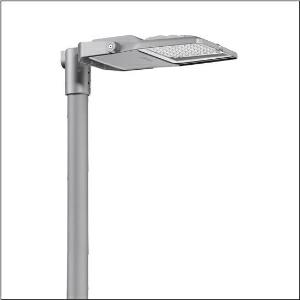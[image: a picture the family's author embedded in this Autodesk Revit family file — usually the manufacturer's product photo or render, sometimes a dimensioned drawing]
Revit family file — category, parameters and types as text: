
# Revit family: floodlight_fl_21_iq_mini___pl43_5xa7771d2a3a_a639
name_source: partatom
category: Lighting Fixtures
units: mm (PartAtom-declared; Revit-internal decimal feet)

## family parameters
Cut with Voids When Loaded = No
Host = Face
Light Source = No
Part Type = Normal
Room Calculation Point = No
Round Connector Dimension = Use Diameter
Shared = No

## types (1)
- --- (1 x LED, 18290 lm, 143 W, 3000K)
    Apparent Load = 143 VA
    CIE Flux Codes = 27 78 99 100 100
    Color Rendering = 70
    Color Temperature = 3000K
    Default Elevation = 1800 mm
    Description = Floodlight FL 21 iQ mini, floodlight, primary light control with lens, of PMMA, primary optical cover: protective disc, of toughened safety glass, transparent, light distribution: PL43, light emission: direct distribution, installation type: surface-mounted, LED, High Power LED, rated luminous flux: 18.290lm, luminous efficacy: 128lm/W, light colour: 730, colour temperature: 3000K, control: Auto-Match, Temp-Guard, Lumen-Switch, Night-Set, Smart-Wire, Light-Fading, Desk-Remote (wireless, voltage-free reading and setting of iQ features in the workshop via application-optimized NFC function/RFID function), optimised constant luminous flux control (CLO 2.0), with terminal, 6-pole, mains connection: 220..240V, AC, 50/60Hz, start of lifetime: 143W, end of service life: 152W, reduction: 61W, luminaire housing, of diecast aluminium, powder-coated, Siteco® metallic grey (DB 702S), corrosivity category C5 mid according to DIN EN ISO 12944, sealing non-destructively replaceable, please order mast flange separately, mast bracket, of steel, galvanised, powder-coated, Siteco® metallic grey (DB 702S), protection rating (complete): IP66, insulation class (complete): insulation class II (safety insulation), certification: CE, ENEC, VDE, protection symbol: D, impact resistance: IK08, permissible operating ambient temperature: -40..+40°C, permissible operating ambient temperature for outdoor applications: -40..+50°C, standard: DIN EN 12944, LABS conformity tested according to VDMA 24364:2018-05, packaging unit: 1 piece

Light Distribution: PL43
    Height = 70 mm
    Lamp = 1 x LED
    Lamp Light Flux = 18290 lm
    Lamp Power = 143 W
    Lamp count = 1
    Length = 485 mm
    Luminous efficacy = 128 lm/W
    Manufacturer = Siteco
    ModVariant = No
    Model = 5XA7771D2A3A
    Number of Poles = 1
    OnlyDefault = Yes
    Power Factor = 1
    Product Name = Floodlight FL 21 iQ mini | PL43
    Product group = floodlight | pylon annexe
    ProductGroupID = 6200
    Protection Class = Protection class II
    Protection Degree = IP 66
    RLX_Detail_Level = 1
    RLX_Emergency_Light_Flux = 0 lm
    RLX_Emergency_Type = 0
    RLX_Emergency_Type_DB = No
    RlxData = <blob elided: 101421 chars, md5=bba395d4>
    Socket = socket
    Standby Power = 0 W
    System Light Flux = 18290 lm
    System Power = 143 W
    Type Comments = factory setting: luminous flux: 100 % | dim-lin: 254 | 730 mA
    Type Image = l_1007125.jpg
    URL = http://relux.com
    VarID = @adj_112017
    Voltage = 0 V
    Weight = 0.00 kg
    Width = 337 mm

## geometry (parser evidence)
native form markers: Blend x4, Sweep x11
no freeform markers — native parametric forms only
